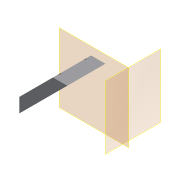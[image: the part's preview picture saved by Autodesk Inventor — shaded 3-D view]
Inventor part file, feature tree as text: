
AUTODESK INVENTOR PART (.ipt)
format: ipt  version: 2019.4 (Build 234330000, 330)  size: 255,488 bytes
history: native  units: mm
features: reference x16, sketch x9, other x9, extrude x8, plane x4, projected_geometry x4, hole x2
ambient origin geometry x8: Origin, YZ Plane, XZ Plane, XY Plane, X Axis, Y Axis, Z Axis, Center Point
bodies: Solid1 (feature_tree)
feature tree (52):
  plane  "Work Plane1"
  extrude  "Extrusion1"  Depth=53.8mm
  extrude  "Extrusion4"  Depth=53.8mm
  hole  "Hole1"  [1 undecoded]
  extrude  "Extrusion5"  Depth=20.0mm
  plane  "Work Plane3"
  sketch  "Sketch7"  dims[d30=20.0mm d31=20.0mm]
  plane  "Work Plane4"
  extrude  "Extrusion6"  Depth=2.8mm
  extrude  "Extrusion7"  Depth=2.8mm
  hole  "Hole2"  [1 undecoded]
  extrude  "Extrusion8"  Depth=0.1mm
  extrude  "Extrusion9"  Depth=8.0mm
  sketch  "Sketch13"  dims[d40=45.0deg d41=8.0mm d42=28.0mm d43=0.0mm d44=30.0mm d45=20.0mm d46=2.9mm d47=6.0mm d48=6.0mm d49=2.5mm d50=90.0deg d51=12.0mm d52=0.0mm d53=2.0mm d54=28.0mm d55=0.0mm d56=2.0mm d57=28.0mm d58=0.0mm d59=15.0mm d60=10.0mm d61=0.0mm d62=2.8mm d64=2.8mm d65=6.0mm d66=5.5mm d67=3.0mm d68=90.0deg d69=12.0mm d70=0.0mm d71=29.0mm d72=0.0mm d73=4.0mm d74=29.0mm d75=0.0mm d76=10.0mm d77=0.0mm]
  plane  "Work Plane5"
  extrude  "Extrusion10"  Depth=10.0mm TaperAngle=0.0deg
  sketch  "Sketch1"  dims[d10=5.0mm d11=0.0mm d18=53.8mm]
  reference  "Reference1"
  reference  "Reference2"
  reference  "Reference3"
  reference  "Reference4"
  reference  "Reference9"
  reference  "Reference20"
  reference  "Reference21"
  reference  "Reference22"
  reference  "Reference23"
  reference  "Reference24"
  sketch  "Sketch4"  dims[d19=45.0deg d20=53.8mm]
  projected_geometry  "Projected Loop1"
  reference  "Reference25"
  reference  "Reference26"
  projected_geometry  "Projected Loop2"
  sketch  "Sketch6"  dims[d21=45.0mm d22=45.0mm]
  reference  "Reference27"
  reference  "Reference28"
  reference  "Reference29"
  reference  "Reference30"
  sketch  "Sketch8"  dims[d32=2.8mm d33=2.8mm]
  sketch  "Sketch9"  dims[d34=2.8mm d35=2.8mm]
  sketch  "Sketch11"  dims[d36=0.1mm d37=0.1mm]
  projected_geometry  "Projected Loop3"
  sketch  "Sketch12"  dims[d38=0.1mm d39=0.1mm]
  projected_geometry  "Projected Loop5"
  other  "Assembly_Cube_v2_Thorlabs.iam"
  other  "10_Cube_Base:1"
  other  "00_Base_v0:1"
  other  "Assembly_Cube_Kinematic_Mirrormount_45_v2.iam"
  other  "Assembly_Cube_empty_1x1_v2:1"
  other  "10_Cube_1x1_v2:1"
  other  "10_Lid_1x1_v2:1"
  other  "DIN 912 - ersetzt durch DIN EN ISO 4762 M3 x 12:7"
  other  "10_Cube_Lid:1"
note: 2 required parameter values undecoded (feature->parameter linkage not recoverable at this tier; creation-order binding heuristic only, values carry confidence <= 0.55)
